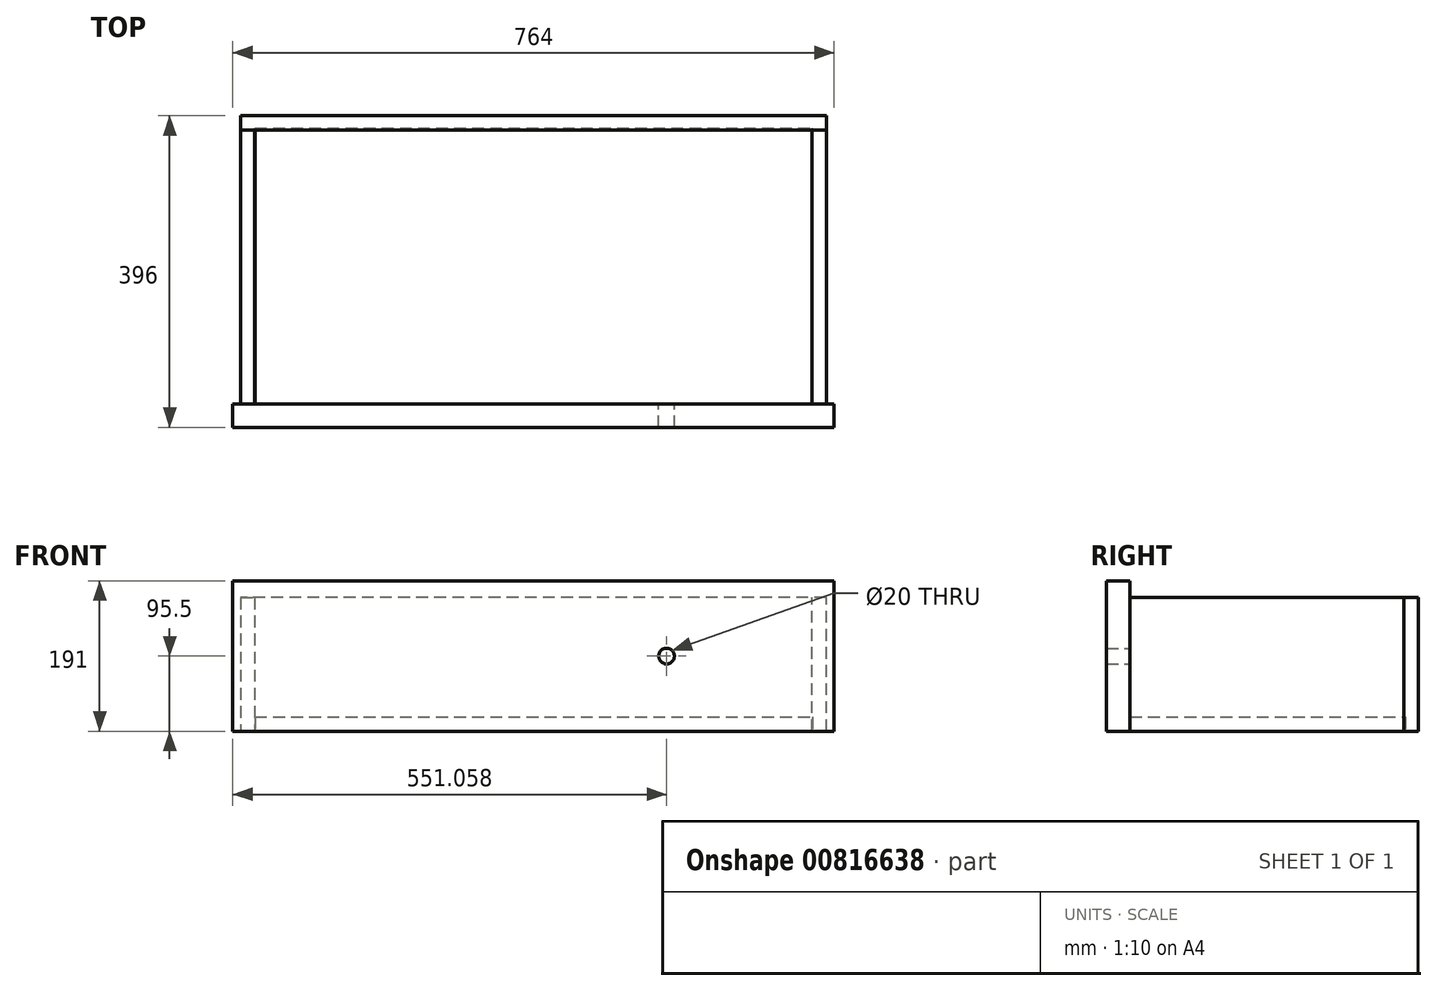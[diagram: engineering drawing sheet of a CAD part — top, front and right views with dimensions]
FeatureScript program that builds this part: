
annotation { "Feature Type Name" : "Feature", "Feature Type Description" : "" }
export const myFeature = defineFeature(function(context is Context, id is Id, definition is map)
    precondition{}
    {
        {
            var Q0;
            Q0=qCreatedBy(makeId("Front.planeOp"),FACE);
            var sketch = newSketch(context, id + "F0", { "sketchPlane" : qUnion([Q0])});
            skLineSegment(sketch, "E0.bottom", {"start": v(-44.1, 191) * mm, "end": v(719.9, 191) * mm});
            skLineSegment(sketch, "E0.top", {"start": v(-44.1, 0) * mm, "end": v(719.9, 0) * mm});
            skLineSegment(sketch, "E0.left", {"start": v(-44.1, 191) * mm, "end": v(-44.1, 0) * mm});
            skLineSegment(sketch, "E0.right", {"start": v(719.9, 191) * mm, "end": v(719.9, 0) * mm});
            skLineSegment(sketch, "E1", {"start": v(337.9, 191) * mm, "end": v(337.9, 0) * mm, "construction": true});
            skLineSegment(sketch, "E2", {"start": v(-44.1, 95.5) * mm, "end": v(719.9, 95.5) * mm, "construction": true});
            skCircle(sketch, "E3", {"center": v(168.85, 95.5) * mm, "radius": 10 * mm});
            skCircle(sketch, "E4.MirrorC", {"center": v(506.96, 95.5) * mm, "radius": 10 * mm});
            skSolve(sketch);
        }
        {
            var Q0;
            Q0=makeQuery(id+"F0.imprint","IMPRINT",FACE,{"disambiguationData":[TD([[makeQuery(id+"F0.imprint","IMPRINT",EDGE,{"derivedFrom":sQuery(id+"F0.wireOp",EDGE,"E0.bottom")}),-1.0]])]});
            extrude(context, id + "F1", {"entities" : qUnion([Q0]), "depth" : 18 * mm, "offsetDistance" : 25 * mm});
        }
        {
            var Q0;
            Q0=makeQuery(id+"F0.imprint","IMPRINT",FACE,{"disambiguationData":[TD([[makeQuery(id+"F0.imprint","IMPRINT",EDGE,{"derivedFrom":sQuery(id+"F0.wireOp",EDGE,"E3")}),1.0]])]});
            var Q1;
            Q1=makeQuery(id+"F0.imprint","IMPRINT",FACE,{"disambiguationData":[TD([[makeQuery(id+"F0.imprint","IMPRINT",EDGE,{"derivedFrom":sQuery(id+"F0.wireOp",EDGE,"E4.MirrorC")}),-1.0]])]});
            extrude(context, id + "F2", {"entities" : qUnion([Q0, Q1]), "operationType" : NewBodyOperationType.ADD, "depth" : 30 * mm, "offsetDistance" : 25 * mm});
        }
        {
            var Q0;
            Q0=qCreatedBy(makeId("Front.planeOp"),FACE);
            var sketch = newSketch(context, id + "F3", { "sketchPlane" : qUnion([Q0])});
            skLineSegment(sketch, "E5.bottom", {"start": v(-34.1, 170) * mm, "end": v(-16.1, 170) * mm});
            skLineSegment(sketch, "E5.top", {"start": v(-34.1, 0) * mm, "end": v(-16.1, 0) * mm});
            skLineSegment(sketch, "E5.left", {"start": v(-34.1, 170) * mm, "end": v(-34.1, 0) * mm});
            skLineSegment(sketch, "E5.right", {"start": v(-16.1, 170) * mm, "end": v(-16.1, 0) * mm});
            skLineSegment(sketch, "E6.bottom", {"start": v(709.9, 0) * mm, "end": v(691.9, 0) * mm});
            skLineSegment(sketch, "E6.top", {"start": v(709.9, 170) * mm, "end": v(691.9, 170) * mm});
            skLineSegment(sketch, "E6.left", {"start": v(709.9, 0) * mm, "end": v(709.9, 170) * mm});
            skLineSegment(sketch, "E6.right", {"start": v(691.9, 0) * mm, "end": v(691.9, 170) * mm});
            skSolve(sketch);
        }
        {
            var Q0;
            Q0=makeQuery(id+"F3.imprint","IMPRINT",FACE,{"disambiguationData":[TD([[makeQuery(id+"F3.imprint","IMPRINT",EDGE,{"derivedFrom":sQuery(id+"F3.wireOp",EDGE,"E5.bottom")}),-1.0]])]});
            var Q1;
            Q1=makeQuery(id+"F3.imprint","IMPRINT",FACE,{"disambiguationData":[TD([[makeQuery(id+"F3.imprint","IMPRINT",EDGE,{"derivedFrom":sQuery(id+"F3.wireOp",EDGE,"E6.bottom")}),-1.0]])]});
            extrude(context, id + "F4", {"entities" : qUnion([Q0, Q1]), "oppositeDirection" : true, "depth" : 348 * mm, "offsetDistance" : 25 * mm});
        }
        {
            var Q0;
            Q0=makeQuery(id+"F4.opExtrude","CAP_FACE",FACE,{"disambiguationData":[OSD([sQuery(id+"F3.wireOp",EDGE,"E6.bottom"),sQuery(id+"F3.wireOp",EDGE,"E6.top"),sQuery(id+"F3.wireOp",EDGE,"E6.left"),sQuery(id+"F3.wireOp",EDGE,"E6.right")])],"isStart":false});
            var sketch = newSketch(context, id + "F5", { "sketchPlane" : qUnion([Q0])});
            skLineSegment(sketch, "E7.bottom", {"start": v(-709.9, 170) * mm, "end": v(33.94, 170) * mm});
            skLineSegment(sketch, "E7.top", {"start": v(-709.9, 0) * mm, "end": v(33.94, 0) * mm});
            skLineSegment(sketch, "E7.left", {"start": v(-709.9, 170) * mm, "end": v(-709.9, 0) * mm});
            skLineSegment(sketch, "E7.right", {"start": v(33.94, 170) * mm, "end": v(33.94, 0) * mm});
            skSolve(sketch);
        }
        {
            var Q0;
            Q0 = qSketchRegion(id + "F5", true);
            extrude(context, id + "F6", {"entities" : qUnion([Q0]), "depth" : 18 * mm, "offsetDistance" : 25 * mm});
        }
        {
            var Q0;
            Q0=qCreatedBy(makeId("Top.planeOp"),FACE);
            var sketch = newSketch(context, id + "F7", { "sketchPlane" : qUnion([Q0])});
            skLineSegment(sketch, "E8.bottom", {"start": v(-15.8, 0) * mm, "end": v(692.51, 0) * mm});
            skLineSegment(sketch, "E8.top", {"start": v(-15.8, 350) * mm, "end": v(692.51, 350) * mm});
            skLineSegment(sketch, "E8.left", {"start": v(-15.8, 0) * mm, "end": v(-15.8, 350) * mm});
            skLineSegment(sketch, "E8.right", {"start": v(692.51, 0) * mm, "end": v(692.51, 350) * mm});
            skSolve(sketch);
        }
        {
            var Q0;
            Q0 = qSketchRegion(id + "F7", true);
            extrude(context, id + "F8", {"entities" : qUnion([Q0]), "depth" : 18 * mm, "offsetDistance" : 25 * mm});
        }
    });
